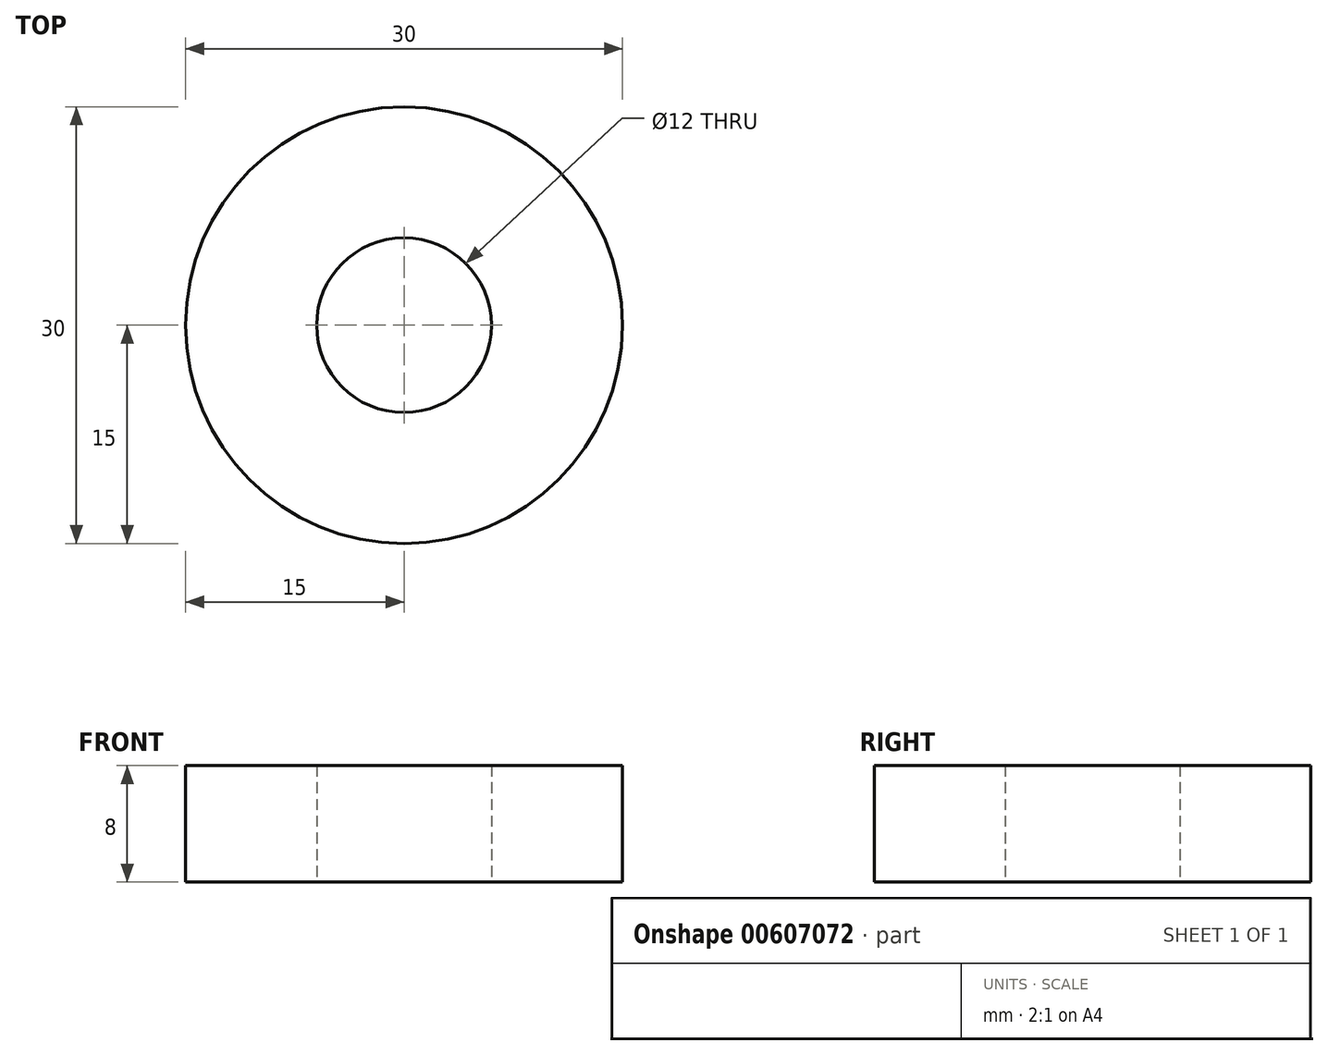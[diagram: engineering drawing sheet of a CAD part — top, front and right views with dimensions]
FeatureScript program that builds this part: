
annotation { "Feature Type Name" : "Feature", "Feature Type Description" : "" }
export const myFeature = defineFeature(function(context is Context, id is Id, definition is map)
    precondition{}
    {
        {
            var Q0;
            Q0=qCreatedBy(makeId("Top.planeOp"),FACE);
            var sketch = newSketch(context, id + "F0", { "sketchPlane" : qUnion([Q0]) });
            skCircle(sketch, "E0", {"center": v(0, 0) * mm, "radius": 15 * mm});
            skCircle(sketch, "E1", {"center": v(0, 0) * mm, "radius": 6 * mm});
            skSolve(sketch);
        }
        {
            var Q0;
            Q0=makeQuery(id+"F0.imprint","IMPRINT",FACE,{"disambiguationData":[TD([[makeQuery(id+"F0.imprint","IMPRINT",EDGE,{"derivedFrom":sQuery(id+"F0.wireOp",EDGE,"E0")}),1.0]])]});
            extrude(context, id + "F1", {"entities" : qUnion([Q0]), "depth" : 8 * mm, "offsetDistance" : 25 * mm});
        }
    });
